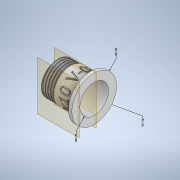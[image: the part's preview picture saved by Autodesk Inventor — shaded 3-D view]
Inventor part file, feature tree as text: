
AUTODESK INVENTOR PART (.ipt)
format: ipt  version: 2021.1 (Build 251245010, 245A)  size: 894,976 bytes
history: native  units: in
note: dims shown in document units (in); Inventor stores cm internally (conversion verified against a paired STEP export)
features: other x4, sketch x3, revolve x1, helix x1, plane x1, emboss x1
ambient origin geometry x8: Origin, YZ Plane, XZ Plane, XY Plane, X Axis, Y Axis, Z Axis, Center Point
bodies: Solid1 (feature_tree)
feature tree (11):
  other  "Annotations"
  revolve  "Revolution1"  [1 undecoded]
  helix  "Coil1"  [1 undecoded]
  plane  "Work Plane2"
  emboss  "Emboss2"
  sketch  "Sketch2"  dims[d0=0.825in d1=0.53in d2=0.125in]
  sketch  "Sketch4"  dims[d3=1.0in]
  sketch  "Sketch6"  dims[d4=90.0deg d5=0.625in d6=0.25in d10=60.0deg d11=0.0072in d12=60.0deg d13=60.0deg d15=0.1in d16=0.2in d17=0.05in d18=0.6144in d19=0.5494in d20=30.0deg d21=0.1in d22=0.625in d23=0.3937in d24=0.0in d25=90.0deg d26=90.0deg d27=0.0in d28=0.0in d38=0.095in d39=0.5494in d40=0.6144in d41=0.25in d42=0.05in d43=0.0in d29=2.0173in d30=1.65in d31=2.2078in d32=1.25in d33=1.04in d34=1.06in]
  other  "Diameter Dimension 1"
  other  "Diameter Dimension 2"
  other  "Diameter Dimension 3"
note: 2 required parameter values undecoded (feature->parameter linkage not recoverable at this tier; creation-order binding heuristic only, values carry confidence <= 0.55)